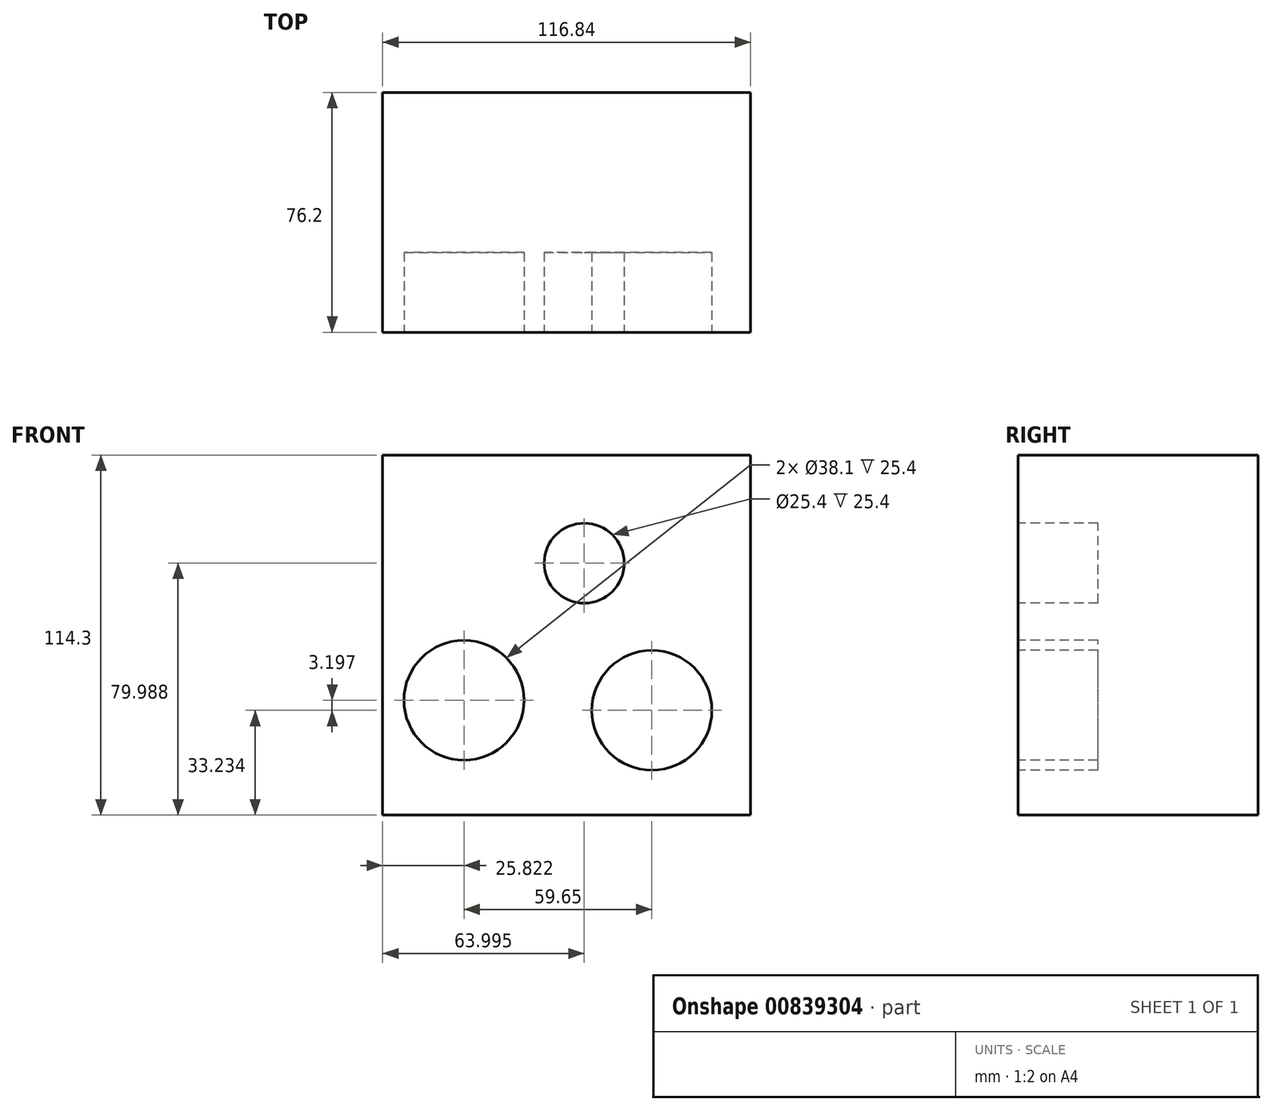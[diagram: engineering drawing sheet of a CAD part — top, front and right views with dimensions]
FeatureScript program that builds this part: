
annotation { "Feature Type Name" : "Feature", "Feature Type Description" : "" }
export const myFeature = defineFeature(function(context is Context, id is Id, definition is map)
    precondition{}
    {
        {
            var Q0;
            Q0=qCreatedBy(makeId("Front.planeOp"),FACE);
            var sketch = newSketch(context, id + "F0", { "sketchPlane" : qUnion([Q0])});
            skLineSegment(sketch, "E0.bottom", {"start": v(-50.8, 38.1) * mm, "end": v(66.04, 38.1) * mm});
            skLineSegment(sketch, "E0.top", {"start": v(-50.8, -76.2) * mm, "end": v(66.04, -76.2) * mm});
            skLineSegment(sketch, "E0.left", {"start": v(-50.8, 38.1) * mm, "end": v(-50.8, -76.2) * mm});
            skLineSegment(sketch, "E0.right", {"start": v(66.04, 38.1) * mm, "end": v(66.04, -76.2) * mm});
            skSolve(sketch);
        }
        {
            var Q0;
            Q0 = qSketchRegion(id + "F0", true);
            extrude(context, id + "F1", {"entities" : qUnion([Q0]), "depth" : 76.2 * mm, "offsetDistance" : 25.4 * mm});
        }
        {
            var Q0;
            Q0=makeQuery(id+"F1.opExtrude","CAP_FACE",FACE,{"disambiguationData":[OSD([sQuery(id+"F0.wireOp",EDGE,"E0.bottom"),sQuery(id+"F0.wireOp",EDGE,"E0.top"),sQuery(id+"F0.wireOp",EDGE,"E0.left"),sQuery(id+"F0.wireOp",EDGE,"E0.right")])],"isStart":false});
            var sketch = newSketch(context, id + "F2", { "sketchPlane" : qUnion([Q0])});
            skCircle(sketch, "E1", {"center": v(13.2, 3.79) * mm, "radius": 12.7 * mm});
            skCircle(sketch, "E2", {"center": v(34.67, -42.97) * mm, "radius": 19.05 * mm});
            skCircle(sketch, "E3", {"center": v(-24.98, -39.77) * mm, "radius": 19.05 * mm});
            skSolve(sketch);
        }
        {
            var Q0;
            Q0 = qSketchRegion(id + "F2", true);
            extrude(context, id + "F3", {"entities" : qUnion([Q0]), "operationType" : NewBodyOperationType.REMOVE, "oppositeDirection" : true, "depth" : 25.4 * mm, "offsetDistance" : 25.4 * mm});
        }
    });
